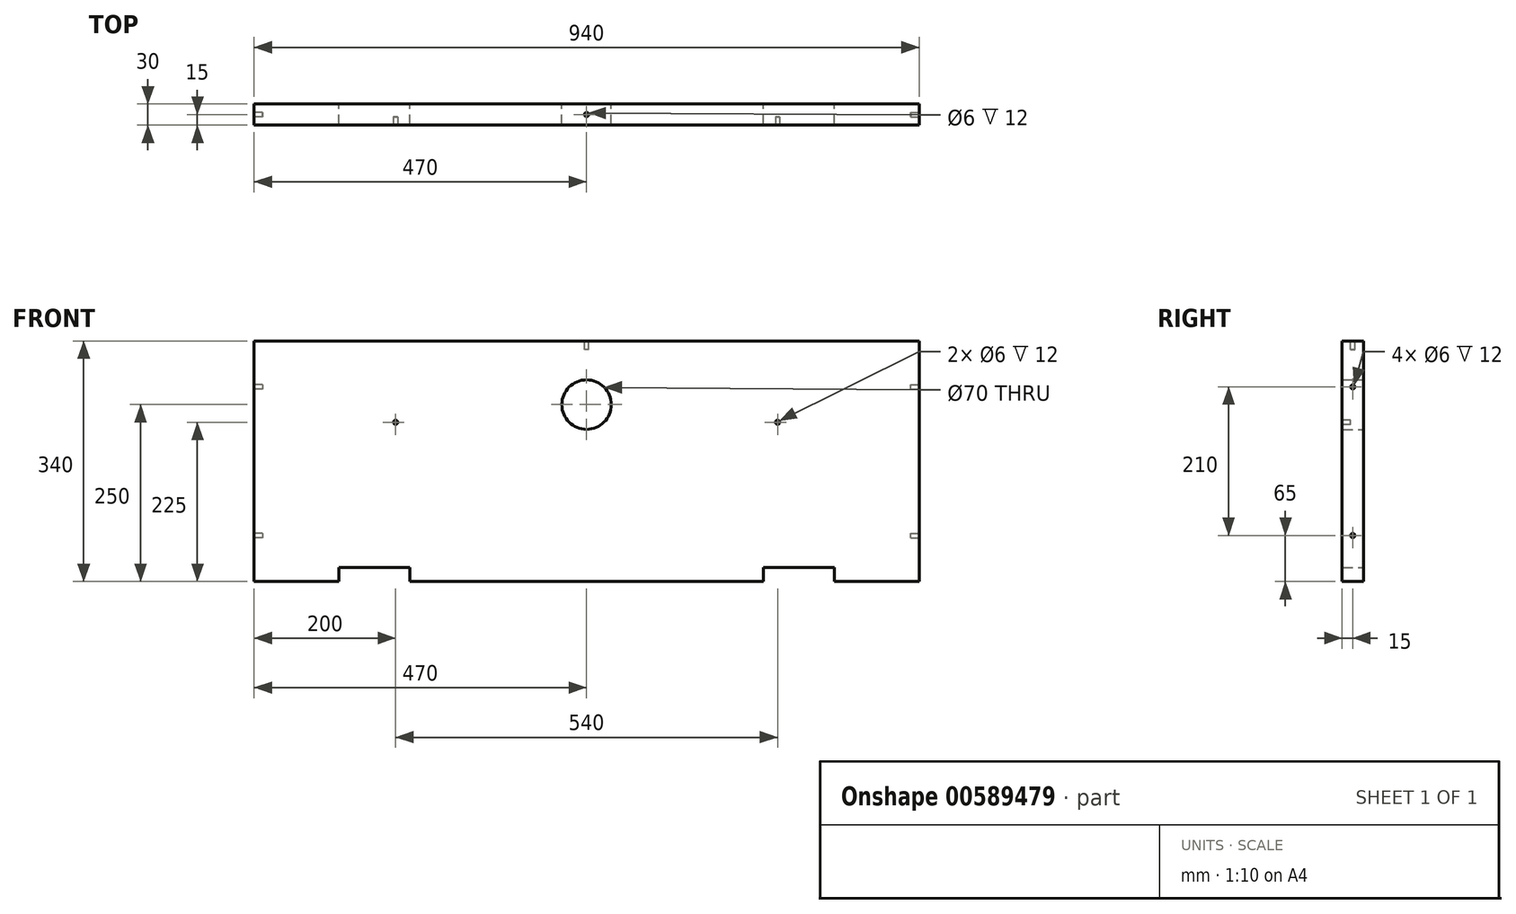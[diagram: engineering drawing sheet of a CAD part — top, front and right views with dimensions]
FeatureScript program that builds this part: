
annotation { "Feature Type Name" : "Feature", "Feature Type Description" : "" }
export const myFeature = defineFeature(function(context is Context, id is Id, definition is map)
    precondition{}
    {
        {
            var Q0;
            Q0=qCreatedBy(makeId("Front.planeOp"),FACE);
            var sketch = newSketch(context, id + "F0", { "sketchPlane" : qUnion([Q0])});
            skLineSegment(sketch, "E0.bottom", {"start": v(0, 0) * mm, "end": v(940, 0) * mm});
            skLineSegment(sketch, "E0.top", {"start": v(0, 340) * mm, "end": v(940, 340) * mm});
            skLineSegment(sketch, "E0.left", {"start": v(0, 0) * mm, "end": v(0, 340) * mm});
            skLineSegment(sketch, "E0.right", {"start": v(940, 0) * mm, "end": v(940, 340) * mm});
            skSolve(sketch);
        }
        {
            var Q0;
            Q0=makeQuery(id+"F0.imprint","IMPRINT",FACE,{"disambiguationData":[TD([[makeQuery(id+"F0.imprint","IMPRINT",EDGE,{"derivedFrom":sQuery(id+"F0.wireOp",EDGE,"E0.bottom")}),1.0]])]});
            extrude(context, id + "F1", {"entities" : qUnion([Q0]), "depth" : 30 * mm, "offsetDistance" : 25 * mm});
        }
        {
            var Q0;
            Q0=makeQuery(id+"F1.opExtrude","SWEPT_FACE",FACE,{"disambiguationData":[OSD([sQuery(id+"F0.wireOp",EDGE,"E0.top")])]});
            var sketch = newSketch(context, id + "F2", { "sketchPlane" : qUnion([Q0])});
            skCircle(sketch, "E1", {"center": v(470, -15) * mm, "radius": 3 * mm});
            skPoint(sketch, "E1.centerSnap0", {"position": v(470, 0) * mm});
            skPoint(sketch, "E1.centerSnap1", {"position": v(940, -15) * mm});
            skSolve(sketch);
        }
        {
            var Q0;
            Q0=makeQuery(id+"F2.imprint","IMPRINT",FACE,{"disambiguationData":[TD([[makeQuery(id+"F2.imprint","IMPRINT",EDGE,{"derivedFrom":sQuery(id+"F2.wireOp",EDGE,"E1")}),1.0]])]});
            extrude(context, id + "F3", {"entities" : qUnion([Q0]), "operationType" : NewBodyOperationType.REMOVE, "oppositeDirection" : true, "depth" : 12 * mm, "offsetDistance" : 25 * mm});
        }
        {
            var Q0;
            Q0=makeQuery(id+"F1.opExtrude","CAP_FACE",FACE,{"disambiguationData":[OSD([sQuery(id+"F0.wireOp",EDGE,"E0.bottom"),sQuery(id+"F0.wireOp",EDGE,"E0.top"),sQuery(id+"F0.wireOp",EDGE,"E0.left"),sQuery(id+"F0.wireOp",EDGE,"E0.right")])],"isStart":true});
            var sketch = newSketch(context, id + "F4", { "sketchPlane" : qUnion([Q0])});
            skLineSegment(sketch, "E2", {"start": v(-820, 0) * mm, "end": v(-820, 20) * mm});
            skLineSegment(sketch, "E3", {"start": v(-820, 20) * mm, "end": v(-720, 20) * mm});
            skLineSegment(sketch, "E4", {"start": v(-720, 20) * mm, "end": v(-720, 0) * mm});
            skSolve(sketch);
        }
        {
            var Q0;
            {var subQ0=sQuery(id+"F4.wireOp",EDGE,"E2");Q0=makeQuery(id+"F4.imprint","IMPRINT",FACE,{"disambiguationData":[TD([[makeQuery(id+"F4.imprint","IMPRINT",EDGE,{"derivedFrom":subQ0}),-1.0]])]});}
            extrude(context, id + "F5", {"entities" : qUnion([Q0]), "operationType" : NewBodyOperationType.REMOVE, "oppositeDirection" : true, "depth" : 30 * mm, "offsetDistance" : 25 * mm});
        }
        {
            var Q0;
            Q0=makeQuery(id+"F1.opExtrude","CAP_FACE",FACE,{"disambiguationData":[OSD([sQuery(id+"F0.wireOp",EDGE,"E0.bottom"),sQuery(id+"F0.wireOp",EDGE,"E0.top"),sQuery(id+"F0.wireOp",EDGE,"E0.left"),sQuery(id+"F0.wireOp",EDGE,"E0.right")])],"isStart":true});
            var sketch = newSketch(context, id + "F6", { "sketchPlane" : qUnion([Q0])});
            skLineSegment(sketch, "E5.bottom", {"start": v(-120, 0) * mm, "end": v(-220, 0) * mm});
            skLineSegment(sketch, "E5.top", {"start": v(-120, 20) * mm, "end": v(-220, 20) * mm});
            skLineSegment(sketch, "E5.left", {"start": v(-120, 0) * mm, "end": v(-120, 20) * mm});
            skLineSegment(sketch, "E5.right", {"start": v(-220, 0) * mm, "end": v(-220, 20) * mm});
            skSolve(sketch);
        }
        {
            var Q0;
            Q0=makeQuery(id+"F6.imprint","IMPRINT",FACE,{"disambiguationData":[TD([[makeQuery(id+"F6.imprint","IMPRINT",EDGE,{"derivedFrom":sQuery(id+"F6.wireOp",EDGE,"E5.bottom")}),-1.0]])]});
            extrude(context, id + "F7", {"entities" : qUnion([Q0]), "operationType" : NewBodyOperationType.REMOVE, "oppositeDirection" : true, "depth" : 30 * mm, "offsetDistance" : 25 * mm});
        }
        {
            var Q0;
            Q0=makeQuery(id+"F1.opExtrude","CAP_FACE",FACE,{"disambiguationData":[OSD([sQuery(id+"F0.wireOp",EDGE,"E0.bottom"),sQuery(id+"F0.wireOp",EDGE,"E0.top"),sQuery(id+"F0.wireOp",EDGE,"E0.left"),sQuery(id+"F0.wireOp",EDGE,"E0.right")])],"isStart":true});
            var sketch = newSketch(context, id + "F8", { "sketchPlane" : qUnion([Q0])});
            skCircle(sketch, "E6", {"center": v(-470, 250) * mm, "radius": 35 * mm});
            skPoint(sketch, "E6.centerSnap0", {"position": v(-470, 340) * mm});
            skSolve(sketch);
        }
        {
            var Q0;
            Q0=makeQuery(id+"F8.imprint","IMPRINT",FACE,{"disambiguationData":[TD([[makeQuery(id+"F8.imprint","IMPRINT",EDGE,{"derivedFrom":sQuery(id+"F8.wireOp",EDGE,"E6")}),1.0]])]});
            extrude(context, id + "F9", {"entities" : qUnion([Q0]), "operationType" : NewBodyOperationType.REMOVE, "oppositeDirection" : true, "depth" : 30 * mm, "offsetDistance" : 25 * mm});
        }
        {
            var Q0;
            Q0=makeQuery(id+"F1.opExtrude","CAP_FACE",FACE,{"disambiguationData":[OSD([sQuery(id+"F0.wireOp",EDGE,"E0.bottom"),sQuery(id+"F0.wireOp",EDGE,"E0.top"),sQuery(id+"F0.wireOp",EDGE,"E0.left"),sQuery(id+"F0.wireOp",EDGE,"E0.right")])],"isStart":false});
            var sketch = newSketch(context, id + "F10", { "sketchPlane" : qUnion([Q0])});
            skCircle(sketch, "E7", {"center": v(740, 225) * mm, "radius": 3 * mm});
            skSolve(sketch);
        }
        {
            var Q0;
            Q0=makeQuery(id+"F1.opExtrude","SWEPT_FACE",FACE,{"disambiguationData":[OSD([sQuery(id+"F0.wireOp",EDGE,"E0.right")])]});
            var sketch = newSketch(context, id + "F11", { "sketchPlane" : qUnion([Q0])});
            skCircle(sketch, "E8", {"center": v(-15, 275) * mm, "radius": 3 * mm});
            skPoint(sketch, "E8.centerSnap0", {"position": v(-15, 340) * mm});
            skCircle(sketch, "E9", {"center": v(-15, 65) * mm, "radius": 3 * mm});
            skPoint(sketch, "E9.centerSnap0", {"position": v(-15, 0) * mm});
            skSolve(sketch);
        }
        {
            var Q0;
            Q0=makeQuery(id+"F11.imprint","IMPRINT",FACE,{"disambiguationData":[TD([[makeQuery(id+"F11.imprint","IMPRINT",EDGE,{"derivedFrom":sQuery(id+"F11.wireOp",EDGE,"E8")}),1.0]])]});
            var Q1;
            Q1=makeQuery(id+"F11.imprint","IMPRINT",FACE,{"disambiguationData":[TD([[makeQuery(id+"F11.imprint","IMPRINT",EDGE,{"derivedFrom":sQuery(id+"F11.wireOp",EDGE,"E9")}),1.0]])]});
            extrude(context, id + "F12", {"entities" : qUnion([Q0, Q1]), "operationType" : NewBodyOperationType.REMOVE, "oppositeDirection" : true, "depth" : 12 * mm, "offsetDistance" : 25 * mm});
        }
        {
            var Q0;
            Q0=makeQuery(id+"F1.opExtrude","SWEPT_FACE",FACE,{"disambiguationData":[OSD([sQuery(id+"F0.wireOp",EDGE,"E0.left")])]});
            var sketch = newSketch(context, id + "F13", { "sketchPlane" : qUnion([Q0])});
            skCircle(sketch, "E10.0", {"center": v(15, 275) * mm, "radius": 3 * mm});
            skLineSegment(sketch, "E11.0.0", {"start": v(0, 0) * mm, "end": v(0, 340) * mm});
            skLineSegment(sketch, "E11.0.1", {"start": v(0, 340) * mm, "end": v(30, 340) * mm});
            skLineSegment(sketch, "E11.0.2", {"start": v(30, 340) * mm, "end": v(30, 0) * mm});
            skLineSegment(sketch, "E11.0.3", {"start": v(30, 0) * mm, "end": v(0, 0) * mm});
            skCircle(sketch, "E12.0", {"center": v(15, 65) * mm, "radius": 3 * mm});
            skSolve(sketch);
        }
        {
            var Q0;
            Q0=makeQuery(id+"F13.imprint","IMPRINT",FACE,{"disambiguationData":[TD([[makeQuery(id+"F13.imprint","IMPRINT",EDGE,{"derivedFrom":sQuery(id+"F13.wireOp",EDGE,"E10.0")}),1.0]])]});
            var Q1;
            Q1=makeQuery(id+"F13.imprint","IMPRINT",FACE,{"disambiguationData":[TD([[makeQuery(id+"F13.imprint","IMPRINT",EDGE,{"derivedFrom":sQuery(id+"F13.wireOp",EDGE,"E12.0")}),1.0]])]});
            var Q2;
            Q2=sQuery(id+"F13.wireOp",EDGE,"E10.0");
            var Q3;
            Q3=sQuery(id+"F13.wireOp",EDGE,"E12.0");
            extrude(context, id + "F14", {"entities" : qUnion([Q0, Q1]), "operationType" : NewBodyOperationType.REMOVE, "surfaceEntities" : qUnion([Q2, Q3]), "oppositeDirection" : true, "depth" : 12 * mm, "offsetDistance" : 25 * mm});
        }
        {
            var Q0;
            Q0=makeQuery(id+"F10.imprint","IMPRINT",FACE,{"disambiguationData":[TD([[makeQuery(id+"F10.imprint","IMPRINT",EDGE,{"derivedFrom":sQuery(id+"F10.wireOp",EDGE,"E7")}),-1.0]])]});
            var sketch = newSketch(context, id + "F15", { "sketchPlane" : qUnion([Q0])});
            skCircle(sketch, "E13", {"center": v(200, 225) * mm, "radius": 3 * mm});
            skSolve(sketch);
        }
        {
            var Q0;
            Q0=makeQuery(id+"F15.imprint","IMPRINT",FACE,{"disambiguationData":[TD([[makeQuery(id+"F15.imprint","IMPRINT",EDGE,{"derivedFrom":makeQuery(id+"F10.imprint","IMPRINT",EDGE,{"derivedFrom":sQuery(id+"F10.wireOp",EDGE,"E7")})}),1.0]])]});
            var Q1;
            Q1=makeQuery(id+"F15.imprint","IMPRINT",FACE,{"disambiguationData":[TD([[makeQuery(id+"F15.imprint","IMPRINT",EDGE,{"derivedFrom":sQuery(id+"F15.wireOp",EDGE,"E13")}),1.0]])]});
            extrude(context, id + "F16", {"entities" : qUnion([Q0, Q1]), "operationType" : NewBodyOperationType.REMOVE, "oppositeDirection" : true, "depth" : 12 * mm, "offsetDistance" : 25 * mm});
        }
    });
